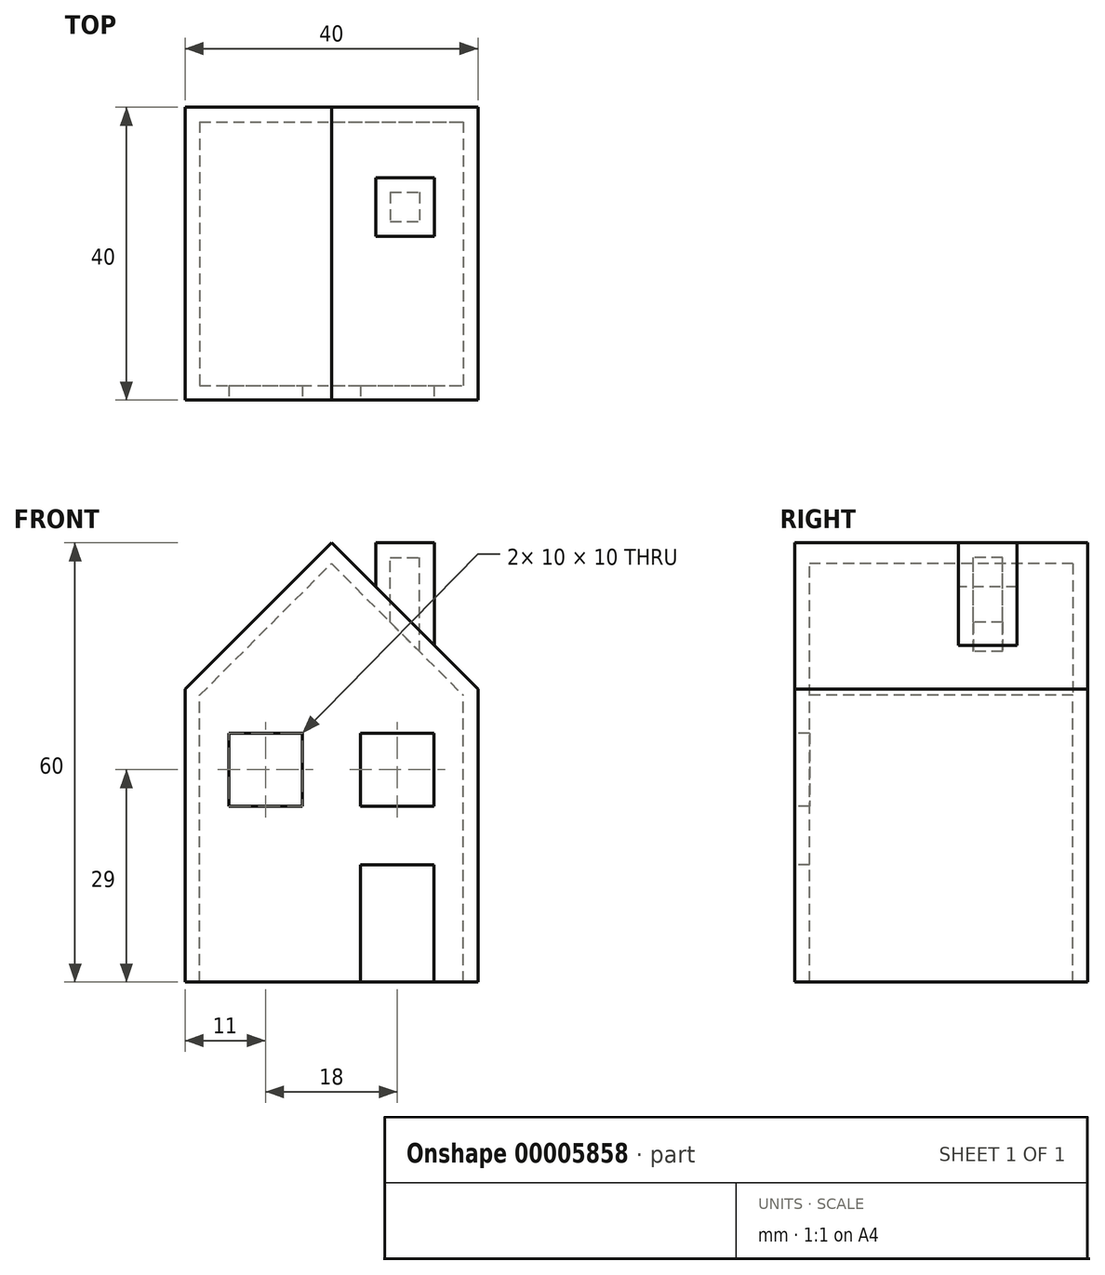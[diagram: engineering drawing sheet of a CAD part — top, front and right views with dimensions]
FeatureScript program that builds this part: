
annotation { "Feature Type Name" : "Feature", "Feature Type Description" : "" }
export const myFeature = defineFeature(function(context is Context, id is Id, definition is map)
    precondition{}
    {
        {
            var Q0;
            Q0=qCreatedBy(makeId("Front.planeOp"),FACE);
            var sketch = newSketch(context, id + "F0", { "sketchPlane" : qUnion([Q0])});
            skLineSegment(sketch, "E0.bottom", {"start": v(0, 0) * mm, "end": v(20, 0) * mm});
            skLineSegment(sketch, "E0.top", {"start": v(0, 20) * mm, "end": v(20, 20) * mm});
            skLineSegment(sketch, "E0.left", {"start": v(0, 0) * mm, "end": v(0, 20) * mm});
            skLineSegment(sketch, "E0.right", {"start": v(20, 0) * mm, "end": v(20, 20) * mm});
            skLineSegment(sketch, "E1", {"start": v(0, 20) * mm, "end": v(10, 30) * mm});
            skLineSegment(sketch, "E2", {"start": v(10, 30) * mm, "end": v(20, 20) * mm});
            skSolve(sketch);
        }
        {
            var Q0;
            Q0=makeQuery(id+"F0.imprint","IMPRINT",FACE,{"disambiguationData":[TD([[makeQuery(id+"F0.imprint","IMPRINT",EDGE,{"derivedFrom":sQuery(id+"F0.wireOp",EDGE,"E0.bottom")}),1.0]])]});
            var Q1;
            Q1=makeQuery(id+"F0.imprint","IMPRINT",FACE,{"disambiguationData":[TD([[makeQuery(id+"F0.imprint","IMPRINT",EDGE,{"derivedFrom":sQuery(id+"F0.wireOp",EDGE,"E0.top")}),1.0]])]});
            extrude(context, id + "F1", {"entities" : qUnion([Q0, Q1]), "oppositeDirection" : true, "depth" : 20 * mm});
        }
        {
            var Q0;
            Q0=makeQuery(id+"F1.opExtrude","SWEPT_FACE",FACE,{"disambiguationData":[OSD([sQuery(id+"F0.wireOp",EDGE,"E0.bottom")])]});
            shell(context, id + "F2", {"entities" : qUnion([Q0]), "thickness" : 2 * mm});
        }
        {
            var Q0;
            Q0=makeQuery(id+"F1.opExtrude","CAP_FACE",FACE,{"disambiguationData":[OSD([sQuery(id+"F0.wireOp",EDGE,"E0.bottom"),sQuery(id+"F0.wireOp",EDGE,"E0.left"),sQuery(id+"F0.wireOp",EDGE,"E0.right"),sQuery(id+"F0.wireOp",EDGE,"E1"),sQuery(id+"F0.wireOp",EDGE,"E2")])],"isStart":true});
            var sketch = newSketch(context, id + "F3", { "sketchPlane" : qUnion([Q0])});
            skLineSegment(sketch, "E3.bottom", {"start": v(12, 0) * mm, "end": v(17, 0) * mm});
            skLineSegment(sketch, "E3.top", {"start": v(12, 8) * mm, "end": v(17, 8) * mm});
            skLineSegment(sketch, "E3.left", {"start": v(12, 0) * mm, "end": v(12, 8) * mm});
            skLineSegment(sketch, "E3.right", {"start": v(17, 0) * mm, "end": v(17, 8) * mm});
            skLineSegment(sketch, "E4.bottom", {"start": v(3, 17) * mm, "end": v(8, 17) * mm});
            skLineSegment(sketch, "E4.top", {"start": v(3, 12) * mm, "end": v(8, 12) * mm});
            skLineSegment(sketch, "E4.left", {"start": v(3, 17) * mm, "end": v(3, 12) * mm});
            skLineSegment(sketch, "E4.right", {"start": v(8, 17) * mm, "end": v(8, 12) * mm});
            skLineSegment(sketch, "E5.bottom", {"start": v(12, 17) * mm, "end": v(17, 17) * mm});
            skLineSegment(sketch, "E5.top", {"start": v(12, 12) * mm, "end": v(17, 12) * mm});
            skLineSegment(sketch, "E5.left", {"start": v(12, 17) * mm, "end": v(12, 12) * mm});
            skLineSegment(sketch, "E5.right", {"start": v(17, 17) * mm, "end": v(17, 12) * mm});
            skSolve(sketch);
        }
        {
            var Q0;
            Q0=makeQuery(id+"F3.imprint","IMPRINT",FACE,{"disambiguationData":[TD([[makeQuery(id+"F3.imprint","IMPRINT",EDGE,{"derivedFrom":sQuery(id+"F3.wireOp",EDGE,"E4.bottom")}),-1.0]])]});
            var Q1;
            Q1=makeQuery(id+"F3.imprint","IMPRINT",FACE,{"disambiguationData":[TD([[makeQuery(id+"F3.imprint","IMPRINT",EDGE,{"derivedFrom":sQuery(id+"F3.wireOp",EDGE,"E5.bottom")}),-1.0]])]});
            var Q2;
            Q2=makeQuery(id+"F3.imprint","IMPRINT",FACE,{"disambiguationData":[TD([[makeQuery(id+"F3.imprint","IMPRINT",EDGE,{"derivedFrom":sQuery(id+"F3.wireOp",EDGE,"E3.bottom")}),1.0]])]});
            var Q3;
            {var subQ0=sQuery(id+"F0.wireOp",EDGE,"E0.bottom");var subQ1=sQuery(id+"F0.wireOp",EDGE,"E0.left");var subQ2=sQuery(id+"F0.wireOp",EDGE,"E0.right");var subQ3=sQuery(id+"F0.wireOp",EDGE,"E1");var subQ4=sQuery(id+"F0.wireOp",EDGE,"E2");Q3=makeQuery(id+"F2.opShell","OFFSET_FACE",FACE,{"disambiguationData":[OSD([subQ0,subQ1,subQ2,subQ3,subQ4]),TDD([makeQuery(id+"F1.opExtrude","CAP_FACE",FACE,{"disambiguationData":[OSD([subQ0,subQ1,subQ2,subQ3,subQ4])],"isStart":false})])]});}
            extrude(context, id + "F4", {"entities" : qUnion([Q0, Q1, Q2]), "operationType" : NewBodyOperationType.REMOVE, "endBound" : BoundingType.UP_TO_SURFACE, "oppositeDirection" : true, "endBoundEntityFace" : qUnion([Q3]), "depth" : 25 * mm});
        }
        {
            var Q0;
            Q0=makeQuery(id+"F1.opExtrude","SWEPT_FACE",FACE,{"disambiguationData":[OSD([sQuery(id+"F0.wireOp",EDGE,"E0.bottom")])]});
            cPlane(context, id + "F5", {"entities" : qUnion([Q0]), "cplaneType" : CPlaneType.OFFSET, "offset" : 30 * mm, "oppositeDirection" : true, "width" : 150 * mm, "height" : 150 * mm});
        }
        {
            var Q0;
            Q0=qCreatedBy(id+"F5.planeOp",FACE);
            var sketch = newSketch(context, id + "F6", { "sketchPlane" : qUnion([Q0])});
            skLineSegment(sketch, "E6.bottom", {"start": v(13.02, -15.19) * mm, "end": v(17.02, -15.19) * mm});
            skLineSegment(sketch, "E6.top", {"start": v(13.02, -11.19) * mm, "end": v(17.02, -11.19) * mm});
            skLineSegment(sketch, "E6.left", {"start": v(13.02, -15.19) * mm, "end": v(13.02, -11.19) * mm});
            skLineSegment(sketch, "E6.right", {"start": v(17.02, -15.19) * mm, "end": v(17.02, -11.19) * mm});
            skSolve(sketch);
        }
        {
            var Q0;
            Q0=makeQuery(id+"F6.imprint","IMPRINT",FACE,{"disambiguationData":[TD([[makeQuery(id+"F6.imprint","IMPRINT",EDGE,{"derivedFrom":sQuery(id+"F6.wireOp",EDGE,"E6.bottom")}),1.0]])]});
            var Q1;
            Q1=makeQuery(id+"F1.opExtrude","SWEPT_FACE",FACE,{"disambiguationData":[OSD([sQuery(id+"F0.wireOp",EDGE,"E2")])]});
            extrude(context, id + "F7", {"entities" : qUnion([Q0]), "operationType" : NewBodyOperationType.ADD, "endBound" : BoundingType.UP_TO_SURFACE, "endBoundEntityFace" : qUnion([Q1]), "depth" : 25 * mm});
        }
        {
            var Q0;
            Q0=makeQuery(id+"F1.opExtrude","SWEPT_BODY",BODY,{"disambiguationData":[OSD([sQuery(id+"F0.wireOp",EDGE,"E0.bottom"),sQuery(id+"F0.wireOp",EDGE,"E0.left"),sQuery(id+"F0.wireOp",EDGE,"E0.right"),sQuery(id+"F0.wireOp",EDGE,"E1"),sQuery(id+"F0.wireOp",EDGE,"E2")])]});
            var Q1;
            Q1=qCreatedBy(makeId("Origin.pointOp"),VERTEX);
            transform(context, id + "F8", {"entities" : qUnion([Q0]), "transformType" : TransformType.SCALE_UNIFORMLY, "scale" : 2, "makeCopy" : false, "scalePoint" : qUnion([Q1])});
        }
        {
            var Q0;
            Q0=makeQuery(id+"F1.opExtrude","CAP_FACE",FACE,{"disambiguationData":[OSD([sQuery(id+"F0.wireOp",EDGE,"E0.bottom"),sQuery(id+"F0.wireOp",EDGE,"E0.left"),sQuery(id+"F0.wireOp",EDGE,"E0.right"),sQuery(id+"F0.wireOp",EDGE,"E1"),sQuery(id+"F0.wireOp",EDGE,"E2")])],"isStart":true});
            var sketch = newSketch(context, id + "F9", { "sketchPlane" : qUnion([Q0])});
            skLineSegment(sketch, "E7.0.0", {"start": v(0, 0) * mm, "end": v(24, 0) * mm, "construction": true});
            skLineSegment(sketch, "E7.0.1", {"start": v(24, 0) * mm, "end": v(24, 16) * mm, "construction": true});
            skLineSegment(sketch, "E7.0.2", {"start": v(24, 16) * mm, "end": v(34, 16) * mm, "construction": true});
            skLineSegment(sketch, "E7.0.3", {"start": v(34, 0) * mm, "end": v(34, 16) * mm, "construction": true});
            skLineSegment(sketch, "E7.0.4", {"start": v(34, 0) * mm, "end": v(40, 0) * mm, "construction": true});
            skLineSegment(sketch, "E7.0.5", {"start": v(40, 0) * mm, "end": v(40, 40) * mm, "construction": true});
            skLineSegment(sketch, "E7.0.6", {"start": v(20, 60) * mm, "end": v(40, 40) * mm, "construction": true});
            skLineSegment(sketch, "E7.0.7", {"start": v(0, 40) * mm, "end": v(20, 60) * mm, "construction": true});
            skLineSegment(sketch, "E7.0.8", {"start": v(0, 0) * mm, "end": v(0, 40) * mm, "construction": true});
            skLineSegment(sketch, "E8.0.0", {"start": v(0, 0) * mm, "end": v(24, 0) * mm});
            skLineSegment(sketch, "E8.0.1", {"start": v(24, 0) * mm, "end": v(24, 16) * mm});
            skLineSegment(sketch, "E8.0.2", {"start": v(24, 16) * mm, "end": v(34, 16) * mm});
            skLineSegment(sketch, "E8.0.3", {"start": v(34, 0) * mm, "end": v(34, 16) * mm});
            skLineSegment(sketch, "E8.0.4", {"start": v(34, 0) * mm, "end": v(40, 0) * mm});
            skLineSegment(sketch, "E8.0.5", {"start": v(40, 0) * mm, "end": v(40, 40) * mm});
            skLineSegment(sketch, "E8.0.6", {"start": v(20, 60) * mm, "end": v(40, 40) * mm});
            skLineSegment(sketch, "E8.0.7", {"start": v(0, 40) * mm, "end": v(20, 60) * mm});
            skLineSegment(sketch, "E8.0.8", {"start": v(0, 0) * mm, "end": v(0, 40) * mm});
            skLineSegment(sketch, "E9.0", {"start": v(24, 34) * mm, "end": v(24, 24) * mm});
            skLineSegment(sketch, "E10.0", {"start": v(24, 24) * mm, "end": v(34, 24) * mm});
            skLineSegment(sketch, "E11.0", {"start": v(34, 34) * mm, "end": v(34, 24) * mm});
            skLineSegment(sketch, "E12.0", {"start": v(24, 34) * mm, "end": v(34, 34) * mm});
            skLineSegment(sketch, "E13.0", {"start": v(6, 34) * mm, "end": v(16, 34) * mm});
            skLineSegment(sketch, "E14.0", {"start": v(6, 34) * mm, "end": v(6, 24) * mm});
            skLineSegment(sketch, "E15.0", {"start": v(16, 34) * mm, "end": v(16, 24) * mm});
            skLineSegment(sketch, "E16.0", {"start": v(6, 24) * mm, "end": v(16, 24) * mm});
            skLineSegment(sketch, "E17", {"start": v(24, 0) * mm, "end": v(34, 0) * mm});
            skSolve(sketch);
        }
        {
            var Q0;
            {var subQ0=sQuery(id+"F0.wireOp",EDGE,"E0.bottom");var subQ1=sQuery(id+"F0.wireOp",EDGE,"E0.left");var subQ2=sQuery(id+"F0.wireOp",EDGE,"E0.right");var subQ3=sQuery(id+"F0.wireOp",EDGE,"E1");var subQ4=sQuery(id+"F0.wireOp",EDGE,"E2");Q0=makeQuery(id+"F2.opShell","OFFSET_FACE",FACE,{"disambiguationData":[OSD([subQ0,subQ1,subQ2,subQ3,subQ4]),TDD([makeQuery(id+"F1.opExtrude","CAP_FACE",FACE,{"disambiguationData":[OSD([subQ0,subQ1,subQ2,subQ3,subQ4])],"isStart":false})])]});}
            var sketch = newSketch(context, id + "F10", { "sketchPlane" : qUnion([Q0])});
            skLineSegment(sketch, "E18.0.0", {"start": v(4, 0) * mm, "end": v(36, 0) * mm});
            skLineSegment(sketch, "E18.0.1", {"start": v(36, 0) * mm, "end": v(36, 38.34) * mm});
            skLineSegment(sketch, "E18.0.2", {"start": v(20, 54.34) * mm, "end": v(36, 38.34) * mm});
            skLineSegment(sketch, "E18.0.3", {"start": v(4, 38.34) * mm, "end": v(20, 54.34) * mm});
            skLineSegment(sketch, "E18.0.4", {"start": v(4, 0) * mm, "end": v(4, 38.34) * mm});
            skSolve(sketch);
        }
        {
            var Q0;
            Q0=makeQuery(id+"F10.imprint","IMPRINT",FACE,{"disambiguationData":[TD([[makeQuery(id+"F10.imprint","IMPRINT",EDGE,{"derivedFrom":sQuery(id+"F10.wireOp",EDGE,"E18.0.0")}),1.0]])]});
            var Q1;
            Q1=makeQuery(id+"F1.opExtrude","CAP_FACE",FACE,{"disambiguationData":[OSD([sQuery(id+"F0.wireOp",EDGE,"E0.bottom"),sQuery(id+"F0.wireOp",EDGE,"E0.left"),sQuery(id+"F0.wireOp",EDGE,"E0.right"),sQuery(id+"F0.wireOp",EDGE,"E1"),sQuery(id+"F0.wireOp",EDGE,"E2")])],"isStart":true});
            extrude(context, id + "F11", {"entities" : qUnion([Q0]), "operationType" : NewBodyOperationType.ADD, "endBound" : BoundingType.UP_TO_SURFACE, "endBoundEntityFace" : qUnion([Q1]), "depth" : 35 * mm});
        }
        {
            var Q0;
            Q0=makeQuery(id+"F11.boolean.opBoolean","MERGE",FACE,{"derivedFrom":[makeQuery(id+"F1.opExtrude","SWEPT_FACE",FACE,{"disambiguationData":[OSD([sQuery(id+"F0.wireOp",EDGE,"E0.bottom")])]}),makeQuery(id+"F11.opExtrude","SWEPT_FACE",FACE,{"disambiguationData":[OSD([sQuery(id+"F10.wireOp",EDGE,"E18.0.0")])]})]});
            shell(context, id + "F12", {"entities" : qUnion([Q0]), "thickness" : 2 * mm});
        }
        {
            var Q0;
            Q0=makeQuery(id+"F9.imprint","IMPRINT",FACE,{"disambiguationData":[TD([[makeQuery(id+"F9.imprint","IMPRINT",EDGE,{"derivedFrom":sQuery(id+"F9.wireOp",EDGE,"E13.0")}),-1.0]])]});
            var Q1;
            Q1=makeQuery(id+"F9.imprint","IMPRINT",FACE,{"disambiguationData":[TD([[makeQuery(id+"F9.imprint","IMPRINT",EDGE,{"derivedFrom":sQuery(id+"F9.wireOp",EDGE,"E9.0")}),1.0]])]});
            var Q2;
            Q2=makeQuery(id+"F9.imprint","IMPRINT",FACE,{"disambiguationData":[TD([[makeQuery(id+"F9.imprint","IMPRINT",EDGE,{"derivedFrom":sQuery(id+"F9.wireOp",EDGE,"E8.0.1")}),-1.0]])]});
            extrude(context, id + "F13", {"entities" : qUnion([Q0, Q1, Q2]), "operationType" : NewBodyOperationType.REMOVE, "oppositeDirection" : true, "depth" : 25 * mm});
        }
    });
